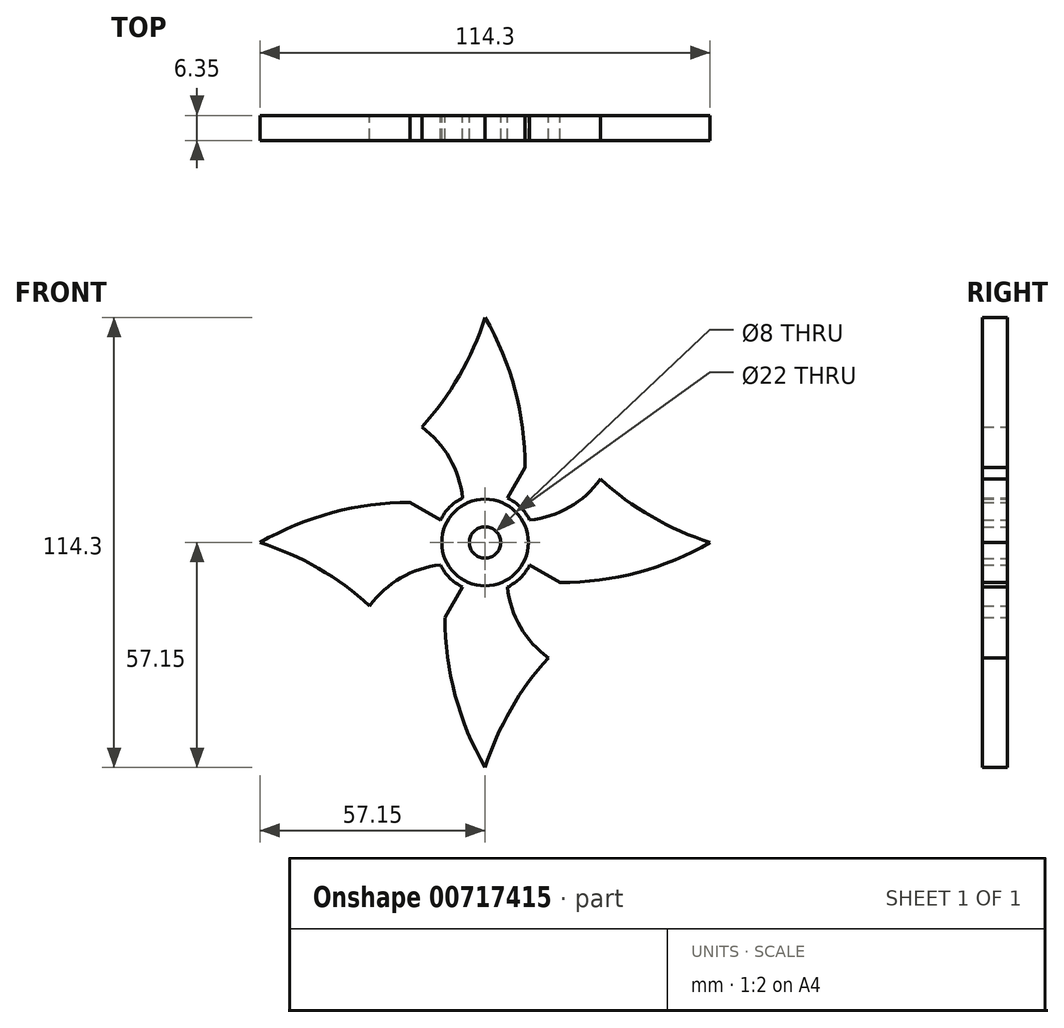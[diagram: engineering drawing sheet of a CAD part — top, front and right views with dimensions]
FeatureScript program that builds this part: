
annotation { "Feature Type Name" : "Feature", "Feature Type Description" : "" }
export const myFeature = defineFeature(function(context is Context, id is Id, definition is map)
    precondition{}
    {
        {
            assignVariable(context, id + "F0", {"name" : "th", "anyValue" : 6.35 * mm});
        }
        {
            var Q0;
            Q0=qCreatedBy(makeId("Front.planeOp"),FACE);
            var sketch = newSketch(context, id + "F1", { "sketchPlane" : qUnion([Q0])});
            skCircle(sketch, "E0", {"center": v(0, 0) * mm, "radius": 12.7 * mm});
            skLineSegment(sketch, "E1", {"start": v(-5.71, 11.34) * mm, "end": v(-16.08, 29.3) * mm, "construction": true});
            skLineSegment(sketch, "E2", {"start": v(-16.08, 29.3) * mm, "end": v(0, 57.15) * mm, "construction": true});
            skLineSegment(sketch, "E3", {"start": v(0, 57.15) * mm, "end": v(10.2, 19.1) * mm, "construction": true});
            skLineSegment(sketch, "E4", {"start": v(10.2, 19.1) * mm, "end": v(5.72, 11.34) * mm});
            skLineSegment(sketch, "E5", {"start": v(0, 57.15) * mm, "end": v(0, 12.7) * mm, "construction": true});
            skLineSegment(sketch, "E6", {"start": v(5.72, 11.34) * mm, "end": v(0, 11.34) * mm, "construction": true});
            skLineSegment(sketch, "E7", {"start": v(0, 11.34) * mm, "end": v(-5.72, 11.34) * mm, "construction": true});
            skArc(sketch, "E8", {"start": v(10.2, 19.1) * mm, "mid": v(7.6, 38.8) * mm, "end": v(0, 57.15) * mm});
            skArc(sketch, "E9", {"start": v(-16.08, 29.3) * mm, "mid": v(-6.55, 42.37) * mm, "end": v(0, 57.15) * mm});
            skArc(sketch, "E10", {"start": v(-5.71, 11.34) * mm, "mid": v(-8.98, 21.42) * mm, "end": v(-16.08, 29.3) * mm});
            skCircle(sketch, "E11", {"center": v(0, 0) * mm, "radius": 11 * mm});
            skSolve(sketch);
        }
        {
            var Q0;
            Q0 = qSketchRegion(id + "F1", true);
            extrude(context, id + "F2", {"entities" : qUnion([Q0]), "depth" : getVariable(context, 'th'), "offsetDistance" : 25.4 * mm});
        }
        {
            var Q0;
            Q0=makeQuery(id+"F2.opExtrude","SWEPT_BODY",BODY,{"disambiguationData":[OSD([sQuery(id+"F1.wireOp",EDGE,"E0"),sQuery(id+"F1.wireOp",EDGE,"E4"),sQuery(id+"F1.wireOp",EDGE,"E8"),sQuery(id+"F1.wireOp",EDGE,"E9"),sQuery(id+"F1.wireOp",EDGE,"E10"),sQuery(id+"F1.wireOp",EDGE,"E11")])]});
            var Q1;
            Q1=makeQuery(id+"F2.opExtrude","CAP_EDGE",EDGE,{"disambiguationData":[OSD([sQuery(id+"F1.wireOp",EDGE,"E11")])],"isStart":false});
            circularPattern(context, id + "F3", {"operationType" : NewBodyOperationType.ADD, "entities" : qUnion([Q0]), "axis" : qUnion([Q1]), "angle" : 360 * degree, "instanceCount" : 4, "equalSpace" : true});
        }
        {
            var Q0;
            Q0=qCreatedBy(makeId("Front.planeOp"),FACE);
            var sketch = newSketch(context, id + "F4", { "sketchPlane" : qUnion([Q0])});
            skCircle(sketch, "E12", {"center": v(0, 0) * mm, "radius": 11 * mm});
            skCircle(sketch, "E13", {"center": v(0, 0) * mm, "radius": 4 * mm});
            skSolve(sketch);
        }
        {
            var Q0;
            Q0 = qSketchRegion(id + "F4", true);
            extrude(context, id + "F5", {"entities" : qUnion([Q0]), "depth" : getVariable(context, 'th'), "offsetDistance" : 25.4 * mm});
        }
    });
